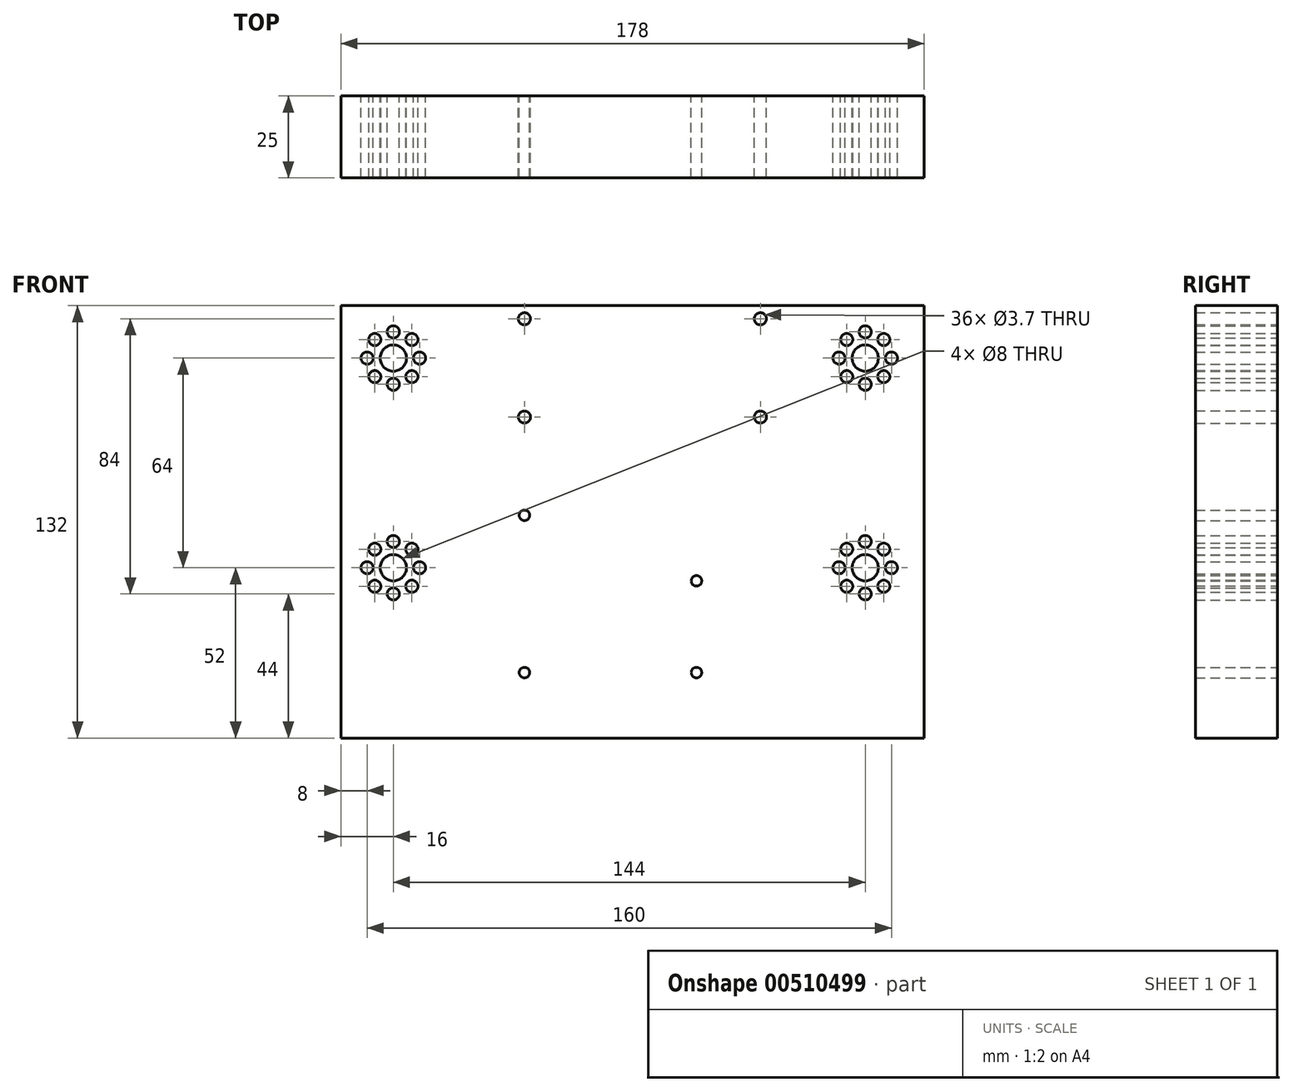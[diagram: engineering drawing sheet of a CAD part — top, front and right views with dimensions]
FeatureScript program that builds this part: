
annotation { "Feature Type Name" : "Feature", "Feature Type Description" : "" }
export const myFeature = defineFeature(function(context is Context, id is Id, definition is map)
    precondition{}
    {
        {
            var Q0;
            Q0=qCreatedBy(makeId("Front.planeOp"),FACE);
            var sketch = newSketch(context, id + "F0", { "sketchPlane" : qUnion([Q0])});
            skLineSegment(sketch, "E0.bottom", {"start": v(-89, 0) * mm, "end": v(89, 0) * mm});
            skLineSegment(sketch, "E0.top", {"start": v(-89, -132) * mm, "end": v(89, -132) * mm});
            skLineSegment(sketch, "E0.left", {"start": v(-89, 0) * mm, "end": v(-89, -132) * mm});
            skLineSegment(sketch, "E0.right", {"start": v(89, 0) * mm, "end": v(89, -132) * mm});
            skCircle(sketch, "E1", {"center": v(-73, -16) * mm, "radius": 4 * mm});
            skCircle(sketch, "E2", {"center": v(-73, -24) * mm, "radius": 1.85 * mm});
            skCircle(sketch, "E3.1.0", {"center": v(-67.34, -21.66) * mm, "radius": 1.85 * mm});
            skCircle(sketch, "E3.2.0", {"center": v(-65, -16) * mm, "radius": 1.85 * mm});
            skCircle(sketch, "E3.3.0", {"center": v(-67.34, -10.34) * mm, "radius": 1.85 * mm});
            skCircle(sketch, "E3.4.0", {"center": v(-73, -8) * mm, "radius": 1.85 * mm});
            skCircle(sketch, "E3.5.0", {"center": v(-78.66, -10.34) * mm, "radius": 1.85 * mm});
            skCircle(sketch, "E3.6.0", {"center": v(-81, -16) * mm, "radius": 1.85 * mm});
            skCircle(sketch, "E3.7.0", {"center": v(-78.66, -21.66) * mm, "radius": 1.85 * mm});
            skCircle(sketch, "E4.0.1.0", {"center": v(-73, -80) * mm, "radius": 4 * mm});
            skPoint(sketch, "E4.0.1.1", {"position": v(-73, -80) * mm});
            skCircle(sketch, "E4.0.1.2", {"center": v(-73, -88) * mm, "radius": 1.85 * mm});
            skCircle(sketch, "E4.0.1.3", {"center": v(-67.34, -85.66) * mm, "radius": 1.85 * mm});
            skCircle(sketch, "E4.0.1.4", {"center": v(-65, -80) * mm, "radius": 1.85 * mm});
            skCircle(sketch, "E4.0.1.5", {"center": v(-67.34, -74.34) * mm, "radius": 1.85 * mm});
            skCircle(sketch, "E4.0.1.6", {"center": v(-78.66, -74.34) * mm, "radius": 1.85 * mm});
            skCircle(sketch, "E4.0.1.7", {"center": v(-73, -72) * mm, "radius": 1.85 * mm});
            skCircle(sketch, "E4.0.1.8", {"center": v(-81, -80) * mm, "radius": 1.85 * mm});
            skCircle(sketch, "E4.0.1.9", {"center": v(-78.66, -85.66) * mm, "radius": 1.85 * mm});
            skCircle(sketch, "E4.1.0.0", {"center": v(71, -16) * mm, "radius": 4 * mm});
            skPoint(sketch, "E4.1.0.1", {"position": v(71, -16) * mm});
            skCircle(sketch, "E4.1.0.2", {"center": v(71, -24) * mm, "radius": 1.85 * mm});
            skCircle(sketch, "E4.1.0.3", {"center": v(76.66, -21.66) * mm, "radius": 1.85 * mm});
            skCircle(sketch, "E4.1.0.4", {"center": v(79, -16) * mm, "radius": 1.85 * mm});
            skCircle(sketch, "E4.1.0.5", {"center": v(76.66, -10.34) * mm, "radius": 1.85 * mm});
            skCircle(sketch, "E4.1.0.6", {"center": v(65.34, -10.34) * mm, "radius": 1.85 * mm});
            skCircle(sketch, "E4.1.0.7", {"center": v(71, -8) * mm, "radius": 1.85 * mm});
            skCircle(sketch, "E4.1.0.8", {"center": v(63, -16) * mm, "radius": 1.85 * mm});
            skCircle(sketch, "E4.1.0.9", {"center": v(65.34, -21.66) * mm, "radius": 1.85 * mm});
            skCircle(sketch, "E4.1.1.0", {"center": v(71, -80) * mm, "radius": 4 * mm});
            skPoint(sketch, "E4.1.1.1", {"position": v(71, -80) * mm});
            skCircle(sketch, "E4.1.1.2", {"center": v(71, -88) * mm, "radius": 1.85 * mm});
            skCircle(sketch, "E4.1.1.3", {"center": v(76.66, -85.66) * mm, "radius": 1.85 * mm});
            skCircle(sketch, "E4.1.1.4", {"center": v(79, -80) * mm, "radius": 1.85 * mm});
            skCircle(sketch, "E4.1.1.5", {"center": v(76.66, -74.34) * mm, "radius": 1.85 * mm});
            skCircle(sketch, "E4.1.1.6", {"center": v(65.34, -74.34) * mm, "radius": 1.85 * mm});
            skCircle(sketch, "E4.1.1.7", {"center": v(71, -72) * mm, "radius": 1.85 * mm});
            skCircle(sketch, "E4.1.1.8", {"center": v(63, -80) * mm, "radius": 1.85 * mm});
            skCircle(sketch, "E4.1.1.9", {"center": v(65.34, -85.66) * mm, "radius": 1.85 * mm});
            skLineSegment(sketch, "E4.direction1", {"start": v(-78.66, -21.66) * mm, "end": v(65.34, -21.66) * mm, "construction": true});
            skLineSegment(sketch, "E4.direction2", {"start": v(-78.66, -21.66) * mm, "end": v(-78.66, -85.66) * mm, "construction": true});
            skCircle(sketch, "E5", {"center": v(-33, -4) * mm, "radius": 1.85 * mm});
            skCircle(sketch, "E6", {"center": v(39, -4) * mm, "radius": 1.85 * mm});
            skCircle(sketch, "E7", {"center": v(39, -34) * mm, "radius": 1.85 * mm});
            skCircle(sketch, "E8", {"center": v(-33, -34) * mm, "radius": 1.85 * mm});
            skLineSegment(sketch, "E9.direction1", {"start": v(-81.6, -11.8) * mm, "end": v(62.4, -11.8) * mm, "construction": true});
            skCircle(sketch, "E10", {"center": v(-33, -64) * mm, "radius": 1.6 * mm});
            skCircle(sketch, "E11", {"center": v(19.5, -84) * mm, "radius": 1.6 * mm});
            skCircle(sketch, "E12", {"center": v(19.5, -112) * mm, "radius": 1.6 * mm});
            skCircle(sketch, "E13", {"center": v(-33, -112) * mm, "radius": 1.6 * mm});
            skSolve(sketch);
        }
        {
            var Q0;
            Q0=makeQuery(id+"F0.imprint","IMPRINT",FACE,{"disambiguationData":[TD([[makeQuery(id+"F0.imprint","IMPRINT",EDGE,{"derivedFrom":sQuery(id+"F0.wireOp",EDGE,"E0.bottom")}),-1.0]])]});
            extrude(context, id + "F1", {"entities" : qUnion([Q0]), "depth" : 25 * mm, "offsetDistance" : 25 * mm});
        }
    });
